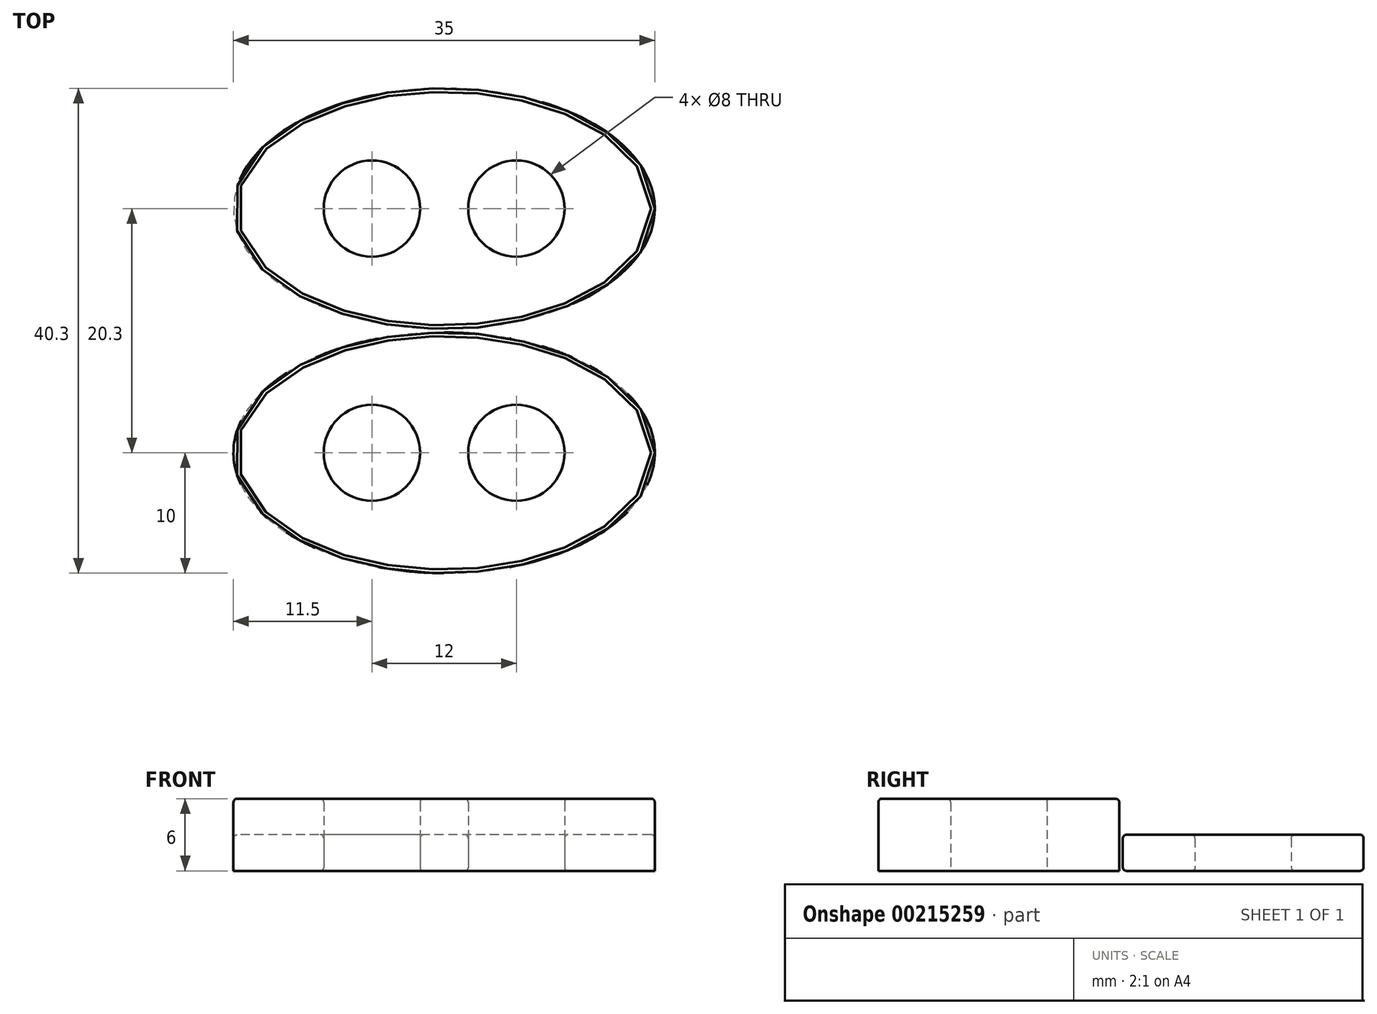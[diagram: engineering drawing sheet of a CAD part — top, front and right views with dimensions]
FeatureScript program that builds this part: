
annotation { "Feature Type Name" : "Feature", "Feature Type Description" : "" }
export const myFeature = defineFeature(function(context is Context, id is Id, definition is map)
    precondition{}
    {
        {
            assignVariable(context, id + "F0", {"name" : "PrintOffset", "anyValue" : 0.3});
        }
        {
            assignVariable(context, id + "F1", {"name" : "Height", "anyValue" : 20});
        }
        {
            assignVariable(context, id + "F2", {"name" : "WallThickness", "anyValue" : 3});
        }
        {
            var Q0;
            Q0=qCreatedBy(makeId("Top.planeOp"),FACE);
            var sketch = newSketch(context, id + "F3", { "sketchPlane" : qUnion([Q0])});
            skCircle(sketch, "E0", {"center": v(-6, 0) * mm, "radius": 4 * mm});
            skLineSegment(sketch, "E1", {"start": v(0, 10) * mm, "end": v(0, -10) * mm, "construction": true});
            skCircle(sketch, "E2.MirrorC", {"center": v(6, 0) * mm, "radius": 4 * mm});
            skEllipse(sketch, "E3", {"center": v(0, 0) * mm, "majorRadius": 17.5 * mm, "minorRadius": 10 * mm, "majorAxis": v(1, 0)});
            skFitSpline(sketch, "E4.0", {"points": [v(14.4, -0.94) * mm, v(14.55, 0) * mm, v(14.4, 0.94) * mm, v(13.93, 1.86) * mm, v(13.27, 2.66) * mm, v(12.4, 3.48) * mm, v(10.97, 4.5) * mm, v(9.1, 5.37) * mm, v(7.38, 5.96) * mm, v(5.56, 6.46) * mm, v(3.6, 6.8) * mm, v(1.56, 6.97) * mm, v(0, 7.01) * mm, v(-1.56, 6.97) * mm, v(-3.6, 6.8) * mm, v(-5.56, 6.46) * mm, v(-7.38, 5.96) * mm, v(-9.1, 5.37) * mm, v(-10.97, 4.5) * mm, v(-12.4, 3.48) * mm, v(-13.27, 2.66) * mm, v(-13.93, 1.86) * mm, v(-14.4, 0.94) * mm, v(-14.55, 0) * mm, v(-14.4, -0.94) * mm, v(-13.93, -1.86) * mm, v(-13.27, -2.66) * mm, v(-12.4, -3.48) * mm, v(-10.97, -4.5) * mm, v(-9.1, -5.37) * mm, v(-7.38, -5.96) * mm, v(-5.56, -6.46) * mm, v(-3.6, -6.8) * mm, v(-1.56, -6.97) * mm, v(0, -7.01) * mm, v(1.56, -6.97) * mm, v(3.6, -6.8) * mm, v(5.56, -6.46) * mm, v(7.38, -5.96) * mm, v(9.1, -5.37) * mm, v(10.97, -4.5) * mm, v(12.4, -3.48) * mm, v(13.27, -2.66) * mm, v(13.93, -1.86) * mm, v(14.4, -0.94) * mm, v(14.55, 0) * mm, v(14.4, 0.94) * mm, v(14.4, -0.94) * mm]});
            skFitSpline(sketch, "E5.0", {"points": [v(13.7, -0.17) * mm, v(13.7, 0) * mm, v(13.7, 0.17) * mm, v(13.67, 0.4) * mm, v(13.6, 0.7) * mm, v(13.4, 1.11) * mm, v(13.12, 1.59) * mm, v(12.68, 2.11) * mm, v(11.91, 2.85) * mm, v(10.58, 3.8) * mm, v(8.8, 4.63) * mm, v(7.15, 5.2) * mm, v(5.39, 5.67) * mm, v(3.49, 6) * mm, v(1.51, 6.17) * mm, v(0, 6.21) * mm, v(-1.51, 6.17) * mm, v(-3.49, 6) * mm, v(-5.39, 5.67) * mm, v(-7.15, 5.2) * mm, v(-8.8, 4.63) * mm, v(-10.58, 3.8) * mm, v(-11.91, 2.85) * mm, v(-12.68, 2.11) * mm, v(-13.12, 1.59) * mm, v(-13.4, 1.11) * mm, v(-13.6, 0.7) * mm, v(-13.67, 0.4) * mm, v(-13.7, 0.17) * mm, v(-13.7, 0) * mm, v(-13.7, -0.17) * mm, v(-13.67, -0.4) * mm, v(-13.6, -0.7) * mm, v(-13.4, -1.11) * mm, v(-13.12, -1.59) * mm, v(-12.68, -2.11) * mm, v(-11.91, -2.85) * mm, v(-10.58, -3.8) * mm, v(-8.8, -4.63) * mm, v(-7.15, -5.2) * mm, v(-5.39, -5.67) * mm, v(-3.49, -6) * mm, v(-1.51, -6.17) * mm, v(0, -6.21) * mm, v(1.51, -6.17) * mm, v(3.49, -6) * mm, v(5.39, -5.67) * mm, v(7.15, -5.2) * mm, v(8.8, -4.63) * mm, v(10.58, -3.8) * mm, v(11.91, -2.85) * mm, v(12.68, -2.11) * mm, v(13.12, -1.59) * mm, v(13.4, -1.11) * mm, v(13.6, -0.7) * mm, v(13.67, -0.4) * mm, v(13.7, -0.17) * mm, v(13.7, 0) * mm, v(13.7, 0.17) * mm, v(13.7, -0.17) * mm]});
            skSolve(sketch);
        }
        {
            var Q0;
            Q0=makeQuery(id+"F3.imprint","IMPRINT",FACE,{"disambiguationData":[TD([[makeQuery(id+"F3.imprint","IMPRINT",EDGE,{"derivedFrom":sQuery(id+"F3.wireOp",EDGE,"E3")}),1.0]])]});
            extrude(context, id + "F4", {"entities" : qUnion([Q0]), "depth" : (getVariable(context, 'WallThickness')) * mm});
        }
        {
            var Q0;
            Q0=makeQuery(id+"F4.opExtrude","SWEPT_BODY",BODY,{"disambiguationData":[OSD([sQuery(id+"F3.wireOp",EDGE,"E3"),sQuery(id+"F3.wireOp",EDGE,"E4.0")])]});
            transform(context, id + "F5", {"entities" : qUnion([Q0]), "transformType" : TransformType.TRANSLATION_3D, "dx" : 0 * mm, "dy" : (getVariable(context, 'Height') + getVariable(context, 'PrintOffset')) * mm, "dz" : 0 * mm, "makeCopy" : false});
        }
        {
            var Q0;
            Q0=makeQuery(id+"F3.imprint","IMPRINT",FACE,{"disambiguationData":[TD([[makeQuery(id+"F3.imprint","IMPRINT",EDGE,{"derivedFrom":sQuery(id+"F3.wireOp",EDGE,"E3")}),1.0]])]});
            var Q1;
            Q1=makeQuery(id+"F3.imprint","IMPRINT",FACE,{"disambiguationData":[TD([[makeQuery(id+"F3.imprint","IMPRINT",EDGE,{"derivedFrom":sQuery(id+"F3.wireOp",EDGE,"E4.0")}),1.0]])]});
            extrude(context, id + "F6", {"entities" : qUnion([Q0, Q1]), "depth" : (getVariable(context, 'WallThickness')) * mm});
        }
        {
            var Q0;
            Q0=makeQuery(id+"F3.imprint","IMPRINT",FACE,{"disambiguationData":[TD([[makeQuery(id+"F3.imprint","IMPRINT",EDGE,{"derivedFrom":sQuery(id+"F3.wireOp",EDGE,"E0")}),-1.0]])]});
            extrude(context, id + "F7", {"entities" : qUnion([Q0]), "operationType" : NewBodyOperationType.ADD, "depth" : (getVariable(context, 'WallThickness') * 2) * mm});
        }
        {
            var Q0;
            Q0=makeQuery(id+"F6.opExtrude","CAP_FACE",FACE,{"disambiguationData":[OSD([sQuery(id+"F3.wireOp",EDGE,"E3"),sQuery(id+"F3.wireOp",EDGE,"E5.0")])],"isStart":false});
            var Q1;
            Q1=makeQuery(id+"F7.opExtrude","CAP_FACE",FACE,{"disambiguationData":[OSD([sQuery(id+"F3.wireOp",EDGE,"E0"),sQuery(id+"F3.wireOp",EDGE,"E2.MirrorC"),sQuery(id+"F3.wireOp",EDGE,"E5.0")])],"isStart":false});
            var Q2;
            {var subQ0=sQuery(id+"F3.wireOp",EDGE,"E5.0");Q2=makeQuery(id+"F7.boolean.opBoolean","MERGE",FACE,{"derivedFrom":[makeQuery(id+"F6.opExtrude","CAP_FACE",FACE,{"disambiguationData":[OSD([sQuery(id+"F3.wireOp",EDGE,"E3"),subQ0])],"isStart":true}),makeQuery(id+"F7.opExtrude","CAP_FACE",FACE,{"disambiguationData":[OSD([sQuery(id+"F3.wireOp",EDGE,"E0"),sQuery(id+"F3.wireOp",EDGE,"E2.MirrorC"),subQ0])],"isStart":true})]});}
            var Q3;
            Q3=makeQuery(id+"F4.opExtrude","CAP_FACE",FACE,{"disambiguationData":[OSD([sQuery(id+"F3.wireOp",EDGE,"E3"),sQuery(id+"F3.wireOp",EDGE,"E4.0")])],"isStart":true});
            var Q4;
            Q4=makeQuery(id+"F4.opExtrude","CAP_FACE",FACE,{"disambiguationData":[OSD([sQuery(id+"F3.wireOp",EDGE,"E3"),sQuery(id+"F3.wireOp",EDGE,"E4.0")])],"isStart":false});
            fillet(context, id + "F8", {"entities" : qUnion([Q0, Q1, Q2, Q3, Q4]), "radius" : (getVariable(context, 'PrintOffset')) * mm, "tangentPropagation" : true, "allowEdgeOverflow" : false});
        }
    });
